FCSTD DOCUMENT  (FreeCAD 0.20R29177 +426 (Git))
Label: ASM_TrussPulley
License: All rights reserved
LicenseURL: http://en.wikipedia.org/wiki/All_rights_reserved
objects: App::Link×7, App::DocumentObjectGroup×3, PartDesign::CoordinateSystem×2, App::FeaturePython×1, App::Part×1
note: 2 computed .brp shape members not serialized (recipe doc carries the construction recipe); baked Part::Feature solids carry a one-line shape summary decoded from their .brp
EXTERNAL_REF file=BreakawayHeadBase.FCStd obj=Sketch
EXTERNAL_REF file=BreakawayHeadTruss.FCStd obj=LCS_Origin
EXTERNAL_REF file=BreakawayHeadTruss.FCStd obj=Assembly
EXTERNAL_REF file=BreakawayHeadTruss.FCStd obj=Pad
EXTERNAL_REF file=BreakawayHeadTruss.FCStd obj=Sketch
EXTERNAL_REF file=CablePulley.FCStd obj=LCS_Origin
EXTERNAL_REF file=CablePulley.FCStd obj=Assembly
EXTERNAL_REF file=Bearing608.FCStd obj=LCS_axle
EXTERNAL_REF file=Bearing608.FCStd obj=Part
EXTERNAL_REF file=CablePulleyBearingHub.FCStd obj=LCS_Origin
EXTERNAL_REF file=CablePulleyBearingHub.FCStd obj=Assembly

FEATURE [App::DocumentObjectGroup] Parts
FEATURE [PartDesign::CoordinateSystem] LCS_Origin
  AttacherType = Attacher::AttachEngine3D
  MapMode = 2
  Support = -> [X_Axis]
FEATURE [App::FeaturePython] Variables  # WARN: FeaturePython — macro-defined, semantics opaque (R4)
  Type = App::PropertyContainer
FEATURE [App::DocumentObjectGroup] Constraints
FEATURE [App::DocumentObjectGroup] Configurations
FEATURE [App::Link] BreakawayHeadTruss
  AttachedBy = #LCS_Origin
  AttachedTo = Parent Assembly#LCS_Origin
  AttachmentOffset = pos=(8,0,0) rot=(0.57735,0.57735,0.57735;2.0944rad)
  LinkPlacement = pos=(8,0,0) rot=(0.57735,0.57735,0.57735;2.0944rad)
  LinkedObject = -> <external BreakawayHeadTruss.FCStd>#Assembly
  Placement = pos=(8,0,0) rot=(0.57735,0.57735,0.57735;2.0944rad)
  SolverId = Asm4EE
  expr: .AttachmentOffset.Base.x = <<BreakawayHeadBase>>#<<Sketch>>.Constraints.EndWidth / 2
  expr: Placement = LCS_Origin.Placement * AttachmentOffset * BreakawayHeadTruss#LCS_Origin.Placement ^ -1
FEATURE [App::Link] BreakawayHeadTruss001
  AttachedBy = #LCS_Origin
  AttachedTo = Parent Assembly#LCS_Origin
  AttachmentOffset = pos=(-10,0,0) rot=(0.57735,0.57735,0.57735;2.0944rad)
  LinkPlacement = pos=(-10,0,0) rot=(0.57735,0.57735,0.57735;2.0944rad)
  LinkedObject = -> <external BreakawayHeadTruss.FCStd>#Assembly
  Placement = pos=(-10,0,0) rot=(0.57735,0.57735,0.57735;2.0944rad)
  SolverId = Asm4EE
  expr: .AttachmentOffset.Base.x = (<<BreakawayHeadBase>>#<<Sketch>>.Constraints.EndWidth / 2 + <<BreakawayHeadTruss>>#<<Pad>>.Length) * -1
  expr: Placement = LCS_Origin.Placement * AttachmentOffset * BreakawayHeadTruss#LCS_Origin.Placement ^ -1
FEATURE [PartDesign::CoordinateSystem] LCS_Pulley
  AttacherType = Attacher::AttachEngine3D
  AttachmentOffset = pos=(0,180,-29.9096) rot=(0,0,1;0rad)
  MapMode = 2
  Placement = pos=(0,180,-29.9096) rot=(0,0,1;0rad)
  Support = -> [LCS_Origin]
  expr: .AttachmentOffset.Base.y = BreakawayHeadTruss#Sketch.Constraints.TrussLength
  expr: .AttachmentOffset.Base.z = BreakawayHeadTruss#Sketch.Constraints.PulleyHoleOffset * -1
FEATURE [App::Link] CablePulley
  AttachedBy = #LCS_Origin
  AttachedTo = Parent Assembly#LCS_Pulley
  AttachmentOffset = pos=(0,0,0) rot=(0,1,0;1.5708rad)
  LinkPlacement = pos=(0,180,-29.9096) rot=(0,1,0;1.5708rad)
  LinkedObject = -> <external CablePulley.FCStd>#Assembly
  Placement = pos=(0,180,-29.9096) rot=(0,1,0;1.5708rad)
  SolverId = Asm4EE
  expr: Placement = LCS_Pulley.Placement * AttachmentOffset * CablePulley#LCS_Origin.Placement ^ -1
FEATURE [App::Link] PulleyBearing
  AssemblyType = Part::Link
  AttachedBy = #LCS_axle
  AttachedTo = Parent Assembly#LCS_Pulley
  AttachmentOffset = pos=(0,0,0) rot=(0,1,0;1.5708rad)
  LinkPlacement = pos=(0,180,-29.9096) rot=(0,1,0;1.5708rad)
  LinkedObject = -> <external Bearing608.FCStd>#Part
  Placement = pos=(0,180,-29.9096) rot=(0,1,0;1.5708rad)
  SolverId = Asm4EE
  expr: Placement = LCS_Pulley.Placement * AttachmentOffset * Bearing608#LCS_axle.Placement ^ -1
FEATURE [App::Link] CablePulleyBearingHub001
  AttachedBy = #LCS_Origin
  AttachedTo = Parent Assembly#LCS_Pulley
  AttachmentOffset = pos=(3.5,0,0) rot=(0,1,0;4.71239rad)
  LinkPlacement = pos=(3.5,180,-29.9096) rot=(0,1,0;4.71239rad)
  LinkedObject = -> <external CablePulleyBearingHub.FCStd>#Assembly
  Placement = pos=(3.5,180,-29.9096) rot=(0,1,0;4.71239rad)
  SolverId = Asm4EE
  expr: Placement = LCS_Pulley.Placement * AttachmentOffset * CablePulleyBearingHub#LCS_Origin.Placement ^ -1
FEATURE [App::Link] CablePulleyBearingHub002
  AttachedBy = #LCS_Origin
  AttachedTo = Parent Assembly#LCS_Pulley
  AttachmentOffset = pos=(-3.5,0,0) rot=(-0.707107,0,-0.707107;3.14159rad)
  LinkPlacement = pos=(-3.5,180,-29.9096) rot=(-0.707107,0,-0.707107;3.14159rad)
  LinkedObject = -> <external CablePulleyBearingHub.FCStd>#Assembly
  Placement = pos=(-3.5,180,-29.9096) rot=(-0.707107,0,-0.707107;3.14159rad)
  SolverId = Asm4EE
  expr: Placement = LCS_Pulley.Placement * AttachmentOffset * CablePulleyBearingHub#LCS_Origin.Placement ^ -1
FEATURE [App::Link] CablePulley001
  AttachedBy = #LCS_Origin
  AttachedTo = Parent Assembly#LCS_Pulley
  AttachmentOffset = pos=(0,0,0) rot=(0,1,0;-1.5708rad)
  LinkPlacement = pos=(0,180,-29.9096) rot=(0,1,0;4.71239rad)
  LinkedObject = -> <external CablePulley.FCStd>#Assembly
  Placement = pos=(0,180,-29.9096) rot=(0,1,0;4.71239rad)
  SolverId = Asm4EE
  expr: Placement = LCS_Pulley.Placement * AttachmentOffset * CablePulley#LCS_Origin.Placement ^ -1
FEATURE [App::Part] Assembly
  AssemblyType = Part::Link
  Group = -> [LCS_Origin,Variables,Constraints,Configurations,BreakawayHeadTruss,BreakawayHeadTruss001,LCS_Pulley,CablePulley,PulleyBearing,CablePulleyBearingHub001,CablePulleyBearingHub002,CablePulley001]
  Origin = -> Origin
  Type = Assembly

RESOLVED EXTERNAL PARTS (link-assembly join: the EXTERNAL_REF files above that resolve inside this repo's crawl, each included once):
---- part Bearing608.FCStd = doc fcstd_2dd5ca27958f ----
FCSTD DOCUMENT  (FreeCAD 0.20R29177 +426 (Git))
Label: Bearing608
License: All rights reserved
LicenseURL: http://en.wikipedia.org/wiki/All_rights_reserved
objects: Sketcher::SketchObject×1, PartDesign::Revolution×1, PartDesign::Chamfer×1, PartDesign::CoordinateSystem×1, App::Part×1
note: 6 computed .brp shape members not serialized (recipe doc carries the construction recipe); baked Part::Feature solids carry a one-line shape summary decoded from their .brp

FEATURE [Sketcher::SketchObject] Sketch
  FullyConstrained = true
  MapMode = 5
  Placement = pos=(0,0,0) rot=(1,0,0;1.5708rad)
  Support = -> [XZ_Plane]
  sketch-geometry (12):
    g0: LineSegment StartX=4 StartY=-3.5 StartZ=0 EndX=5.75 EndY=-3.5 EndZ=0
    g1: LineSegment StartX=11 StartY=-3.5 StartZ=0 EndX=11 EndY=3.5 EndZ=0
    g2: LineSegment StartX=11 StartY=3.5 StartZ=0 EndX=9.25 EndY=3.5 EndZ=0
    g3: LineSegment StartX=4 StartY=3.5 StartZ=0 EndX=4 EndY=-3.5 EndZ=0
    g4: LineSegment StartX=5.75 StartY=3.5 StartZ=0 EndX=6 EndY=3.25 EndZ=0
    g5: LineSegment StartX=6 StartY=3.25 StartZ=0 EndX=9 EndY=3.25 EndZ=0
    g6: LineSegment StartX=9 StartY=3.25 StartZ=0 EndX=9.25 EndY=3.5 EndZ=0
    g7: LineSegment StartX=5.75 StartY=-3.5 StartZ=0 EndX=6 EndY=-3.25 EndZ=0
    g8: LineSegment StartX=6 StartY=-3.25 StartZ=0 EndX=9 EndY=-3.25 EndZ=0
    g9: LineSegment StartX=9 StartY=-3.25 StartZ=0 EndX=9.25 EndY=-3.5 EndZ=0
    g10: LineSegment StartX=5.75 StartY=3.5 StartZ=0 EndX=4 EndY=3.5 EndZ=0
    g11: LineSegment StartX=9.25 StartY=-3.5 StartZ=0 EndX=11 EndY=-3.5 EndZ=0
  constraints (33):
    c: Coincident(g11,g1)
    c: Coincident(g1,g2)
    c: Coincident(g10,g3)
    c: Coincident(g3,g0)
    c: Horizontal(g0)
    c: Horizontal(g2)
    c: Vertical(g1)
    c: DistanceY(g1) = 7
    c: DistanceX(g0) = 4
    c: DistanceX(g11) = 11
    c: Coincident(g4,g5)
    c: Horizontal(g5)
    c: Coincident(g5,g6)
    c: Coincident(g7,g8)
    c: Horizontal(g8)
    c: Coincident(g8,g9)
    c: Coincident(g2,g6)
    c: Coincident(g10,g4)
    c: Tangent(g2,g10)
    c: Coincident(g0,g7)
    c: Coincident(g11,g9)
    c: Tangent(g0,g11)
    c: Equal(g4,g6)
    c: Equal(g6,g7)
    c: Angle(g10,g4) = 2.35619
    c: DistanceX(g2) = -1.75
    c: DistanceX(g10) = -1.75
    c: Equal(g0,g10)
    c: Equal(g11,g2)
    c: Equal(g9,g7)
    c: Parallel(g9,g4)
    c: DistanceY(g5,g1) = 0.25
    c: Symmetric(g0,g3,g-1)
FEATURE [PartDesign::Revolution] Revolution
  AllowMultiFace = false
  Angle = 360
  Axis = (0,-2e-16,1)
  Base = (0,0,0)
  Placement = pos=(0,0,0) rot=(1,0,0;1.5708rad)
  Profile = -> Sketch
  ReferenceAxis = -> Sketch [V_Axis]
  Reversed = true
FEATURE [PartDesign::Chamfer] Chamfer
  Angle = 45
  Base = -> Revolution [Edge3,Edge2,Edge11,Edge12]
  ChamferType = 0
  FlipDirection = false
  Placement = pos=(0,0,0) rot=(1,0,0;1.5708rad)
  Size = 0.25
  Size2 = 1
  SupportTransform = false
  UseAllEdges = false
FEATURE [PartDesign::CoordinateSystem] LCS_axle
  AttacherType = Attacher::AttachEngine3D
  MapMode = 2
  Support = -> [XY_Plane]
FEATURE [App::Part] Part
  Group = -> [Sketch,Revolution,Chamfer,LCS_axle]
  Origin = -> Origin
---- part BreakawayHeadBase.FCStd = doc fcstd_181b5c8611f0 ----
FCSTD DOCUMENT  (FreeCAD 0.20R29177 +426 (Git))
Label: BreakawayHeadBase
License: All rights reserved
LicenseURL: http://en.wikipedia.org/wiki/All_rights_reserved
objects: Sketcher::SketchObject×5, App::DocumentObjectGroup×4, PartDesign::Pocket×4, Part::FeaturePython×4, PartDesign::CoordinateSystem×2, App::Link×2, App::FeaturePython×1, PartDesign::Pad×1, PartDesign::Body×1, App::Part×1
note: 22 computed .brp shape members not serialized (recipe doc carries the construction recipe); baked Part::Feature solids carry a one-line shape summary decoded from their .brp
EXTERNAL_REF file=EndStopTip.FCStd obj=Sketch003
EXTERNAL_REF file=EndStopTip.FCStd obj=Sketch
EXTERNAL_REF file=BreakawayMagnet.FCStd obj=LCS_Origin
EXTERNAL_REF file=BreakawayMagnet.FCStd obj=Assembly

FEATURE [App::DocumentObjectGroup] Parts
FEATURE [PartDesign::CoordinateSystem] LCS_Origin
  AttacherType = Attacher::AttachEngine3D
  MapMode = 2
  Support = -> [X_Axis]
FEATURE [App::FeaturePython] Variables  # WARN: FeaturePython — macro-defined, semantics opaque (R4)
  Type = App::PropertyContainer
FEATURE [App::DocumentObjectGroup] Constraints
FEATURE [App::DocumentObjectGroup] Configurations
FEATURE [Sketcher::SketchObject] Sketch
  FullyConstrained = true
  MapMode = 5
  Support = -> [XY_Plane001]
  expr: Constraints[9] = <<EndStopTip>>#<<SketchChamfer>>.Constraints.MateWidth
  sketch-geometry (14):
    g0: ArcOfCircle CenterX=-10.567 CenterY=-0.5 CenterZ=0 NormalX=0 NormalY=0 NormalZ=1 AngleXU=0 Radius=0.5 StartAngle=1.5708 EndAngle=3.66519
    g1: LineSegment StartX=-10.567 StartY=0 StartZ=0 EndX=10.567 EndY=0 EndZ=0
    g2: ArcOfCircle CenterX=10.567 CenterY=-0.5 CenterZ=0 NormalX=0 NormalY=0 NormalZ=1 AngleXU=0 Radius=0.5 StartAngle=5.75959 EndAngle=7.85398
    g3: LineSegment StartX=11 StartY=-0.75 StartZ=0 EndX=8 EndY=-5.94615 EndZ=0
    g4: LineSegment StartX=-8 StartY=-5.94615 StartZ=0 EndX=-11 EndY=-0.75 EndZ=0
    g5: GeomPoint X=-11.433 Y=0 Z=0
    g6: LineSegment StartX=-8 StartY=-5.94615 StartZ=0 EndX=-8 EndY=-23 EndZ=0
    g7: LineSegment StartX=-7 StartY=-24 StartZ=0 EndX=7 EndY=-24 EndZ=0
    g8: LineSegment StartX=8 StartY=-23 StartZ=0 EndX=8 EndY=-5.94615 EndZ=0
    g9: GeomPoint X=0 Y=-24 Z=0
    g10: ArcOfCircle CenterX=7 CenterY=-23 CenterZ=0 NormalX=0 NormalY=0 NormalZ=1 AngleXU=0 Radius=1 StartAngle=4.71239 EndAngle=6.28319
    g11: GeomPoint X=8 Y=-24 Z=0
    g12: ArcOfCircle CenterX=-7 CenterY=-23 CenterZ=0 NormalX=0 NormalY=0 NormalZ=1 AngleXU=0 Radius=1 StartAngle=3.14159 EndAngle=4.71239
    g13: GeomPoint X=-8 Y=-24 Z=0
  constraints (32):
    c: Tangent(g0,g1) = 1.5708
    c: Tangent(g1,g2) = 1.5708
    c: Tangent(g2,g3) = 1.5708
    c: Tangent(g4,g0) = 1.5708
    c: Horizontal(g1)
    c: Equal(g0,g2)
    c: PointOnObject(g5,g1)
    c: PointOnObject(g5,g4)
    c: Radius(g0) = 0.5
    c: DistanceX(g0,g2) = 22
    c: Symmetric(g1,g0,g-1)
    c: Vertical(g6)
    c: Horizontal(g7)
    c: Vertical(g8)
    c: Symmetric(g13,g11,g9)
    c: PointOnObject(g9,g-2)
    c: Coincident(g4,g6)
    c: Coincident(g8,g3)
    c: Equal(g4,g3)
    c: Angle(g1,g3) = 1.0472
    c: DistanceX(g13,g11) = 16  'EndWidth'
    c: DistanceY(g11,g-1) = 24  'Length'
    c: PointOnObject(g11,g8)
    c: PointOnObject(g11,g7)
    c: Tangent(g8,g10) = -1.5708
    c: Tangent(g7,g10) = -1.5708
    c: PointOnObject(g13,g7)
    c: PointOnObject(g13,g6)
    c: Tangent(g7,g12) = -1.5708
    c: Tangent(g6,g12) = -1.5708
    c: Equal(g12,g10)
    c: Radius(g10) = 1
FEATURE [PartDesign::Pad] Pad
  Direction = (0,0,1)
  Length = 42
  Length2 = 10
  Midplane = true
  Profile = -> Sketch
  ReferenceAxis = -> Sketch [N_Axis]
  Type = 0
  expr: Length = <<EndStopTip>>#<<Sketch>>.Constraints.Height
FEATURE [Sketcher::SketchObject] Sketch001
  FullyConstrained = true
  MapMode = 5
  Placement = pos=(0,0,0) rot=(0.57735,0.57735,0.57735;2.0944rad)
  Support = -> [YZ_Plane001]
  expr: Constraints[25] = <<Sketch>>.Constraints.Length
  sketch-geometry (9):
    g0: LineSegment StartX=-24 StartY=13 StartZ=0 EndX=-34.7696 EndY=13 EndZ=0
    g1: LineSegment StartX=-34.7696 StartY=13 StartZ=0 EndX=-42.3848 EndY=5.38478 EndZ=0
    g2: LineSegment StartX=-42.3848 StartY=5.38478 StartZ=0 EndX=-42.3848 EndY=-5.38478 EndZ=0
    g3: LineSegment StartX=-42.3848 StartY=-5.38478 StartZ=0 EndX=-34.7696 EndY=-13 EndZ=0
    g4: LineSegment StartX=-34.7696 StartY=-13 StartZ=0 EndX=-24 EndY=-13 EndZ=0
    g5: LineSegment StartX=-24 StartY=-13 StartZ=0 EndX=-16.3848 EndY=-5.38478 EndZ=0
    g6: LineSegment StartX=-16.3848 StartY=-5.38478 StartZ=0 EndX=-16.3848 EndY=5.38478 EndZ=0
    g7: LineSegment StartX=-16.3848 StartY=5.38478 StartZ=0 EndX=-24 EndY=13 EndZ=0
    g8: Circle CenterX=-29.3848 CenterY=0 CenterZ=0 NormalX=0 NormalY=0 NormalZ=1 AngleXU=0 Radius=14.0711
  constraints (21):
    c: Coincident(g0,g1)
    c: Coincident(g1,g2)
    c: Coincident(g2,g3)
    c: Coincident(g3,g4)
    c: Coincident(g4,g5)
    c: Coincident(g5,g6)
    c: Coincident(g6,g7)
    c: Coincident(g7,g0)
    c: Equal(g0, g1-g7) x7
    c: PointOnObject(g0,g8)
    c: PointOnObject(g1,g8)
    c: PointOnObject(g2,g8)
    c: PointOnObject(g3,g8)
    c: PointOnObject(g4,g8)
    c: PointOnObject(g5,g8)
    c: PointOnObject(g6,g8)
    c: PointOnObject(g7,g8)
    c: PointOnObject(g8,g-1)
    c: Horizontal(g0)
    c: DistanceX(g4,g-1) = 24
    c: DistanceY(g3,g0) = 26
FEATURE [PartDesign::Pocket] Pocket  label="Cutout"
  BaseFeature = -> Pad
  Direction = (-1,2e-16,-3e-16)
  Length = 5
  Length2 = 5
  Midplane = true
  Profile = -> Sketch001
  ReferenceAxis = -> Sketch001 [N_Axis]
  Type = 1
FEATURE [Sketcher::SketchObject] Sketch002
  FullyConstrained = true
  MapMode = 5
  Placement = pos=(0,0,0) rot=(0.57735,0.57735,0.57735;2.0944rad)
  Support = -> [YZ_Plane001]
  expr: .Constraints.HolesOffset = <<Sketch>>.Constraints.Length - 6mm
  expr: .Constraints.TrussHoleSpacing = <<Pad>>.Length - 10mm
  sketch-geometry (12):
    g0: LineSegment StartX=-18 StartY=16 StartZ=0 EndX=-18 EndY=-16 EndZ=0
    g1: GeomPoint X=-18 Y=0 Z=0
    g2: ArcOfCircle CenterX=-18 CenterY=16 CenterZ=0 NormalX=0 NormalY=0 NormalZ=1 AngleXU=0 Radius=2.15 StartAngle=2.35619 EndAngle=7.06858
    g3: LineSegment StartX=-19.5203 StartY=17.5203 StartZ=0 EndX=-18.8906 EndY=18.15 EndZ=0
    g4: LineSegment StartX=-16.4797 StartY=17.5203 StartZ=0 EndX=-17.1094 EndY=18.15 EndZ=0
    g5: LineSegment StartX=-17.1094 StartY=18.15 StartZ=0 EndX=-18.8906 EndY=18.15 EndZ=0
    g6: ArcOfCircle CenterX=-18 CenterY=16 CenterZ=0 NormalX=0 NormalY=0 NormalZ=1 AngleXU=0 Radius=2.15 StartAngle=0.785398 EndAngle=2.35619
    g7: ArcOfCircle CenterX=-18 CenterY=-16 CenterZ=0 NormalX=0 NormalY=0 NormalZ=1 AngleXU=0 Radius=2.15 StartAngle=2.35619 EndAngle=7.06858
    g8: LineSegment StartX=-19.5203 StartY=-14.4797 StartZ=0 EndX=-18.8906 EndY=-13.85 EndZ=0
    g9: LineSegment StartX=-16.4797 StartY=-14.4797 StartZ=0 EndX=-17.1094 EndY=-13.85 EndZ=0
    g10: LineSegment StartX=-17.1094 StartY=-13.85 StartZ=0 EndX=-18.8906 EndY=-13.85 EndZ=0
    g11: ArcOfCircle CenterX=-18 CenterY=-16 CenterZ=0 NormalX=0 NormalY=0 NormalZ=1 AngleXU=0 Radius=2.15 StartAngle=0.785398 EndAngle=2.35619
  constraints (31):
    c: Vertical(g0)
    c: PointOnObject(g1,g-1)
    c: DistanceY(g0,g0) = 32  'TrussHoleSpacing'
    c: DistanceX(g1,g-1) = 18  'HolesOffset'
    c: Coincident(g2,g0)
    c: Symmetric(g2,g0,g1)
    c: Coincident(g5,g4)
    c: Coincident(g5,g3)
    c: Horizontal(g5)
    c: Tangent(g4,g2) = -1.5708
    c: Tangent(g3,g2) = 1.5708
    c: Diameter(g2) = 4.3
    c: Coincident(g6,g2)
    c: Coincident(g6,g2)
    c: Coincident(g6,g2)
    c: Tangent(g5,g6)
    c: Equal(g4,g3)
    c: Angle(g5,g4) = 2.35619
    c: Coincident(g10,g9)
    c: Coincident(g10,g8)
    c: Horizontal(g10)
    c: Tangent(g9,g7) = -1.5708
    c: Tangent(g8,g7) = 1.5708
    c: Equal(g2,g7) = 5.4
    c: Coincident(g11,g7)
    c: Coincident(g11,g7)
    c: Coincident(g11,g7)
    c: Tangent(g10,g11)
    c: Equal(g9,g8)
    c: Angle(g10,g9) = 2.35619
    c: Coincident(g7,g0)
FEATURE [PartDesign::Pocket] Pocket001  label="TrussHoles"
  BaseFeature = -> Pocket
  Direction = (-1,2e-16,-3e-16)
  Length = 5
  Length2 = 5
  Midplane = true
  Profile = -> Sketch002
  ReferenceAxis = -> Sketch002 [N_Axis]
  Type = 1
FEATURE [Sketcher::SketchObject] Sketch003
  FullyConstrained = true
  MapMode = 5
  Placement = pos=(0,0,0) rot=(1,0,0;1.5708rad)
  Support = -> [XZ_Plane001]
  sketch-geometry (13):
    g0: ArcOfCircle CenterX=0 CenterY=10 CenterZ=0 NormalX=0 NormalY=0 NormalZ=1 AngleXU=0 Radius=9.25 StartAngle=2.35619 EndAngle=3.92699
    g1: ArcOfCircle CenterX=0 CenterY=10 CenterZ=0 NormalX=0 NormalY=0 NormalZ=1 AngleXU=0 Radius=9.25 StartAngle=5.49779 EndAngle=7.06858
    g2: ArcOfCircle CenterX=-9e-16 CenterY=-10 CenterZ=0 NormalX=0 NormalY=0 NormalZ=1 AngleXU=0 Radius=9.25 StartAngle=5.49779 EndAngle=7.06858
    g3: ArcOfCircle CenterX=-9e-16 CenterY=-10 CenterZ=0 NormalX=0 NormalY=0 NormalZ=1 AngleXU=0 Radius=9.25 StartAngle=2.35619 EndAngle=3.92699
    g4: LineSegment StartX=-6.54074 StartY=3.45926 StartZ=0 EndX=-6.54074 EndY=-3.45926 EndZ=0
    g5: LineSegment StartX=6.54074 StartY=3.45926 StartZ=0 EndX=6.54074 EndY=-3.45926 EndZ=0
    g6: LineSegment StartX=6.54074 StartY=-16.5407 StartZ=0 EndX=6.54074 EndY=-22.5407 EndZ=0
    g7: LineSegment StartX=6.54074 StartY=-22.5407 StartZ=0 EndX=-6.54074 EndY=-22.5407 EndZ=0
    g8: LineSegment StartX=-6.54074 StartY=-22.5407 StartZ=0 EndX=-6.54074 EndY=-16.5407 EndZ=0
    g9: LineSegment StartX=-6.54074 StartY=16.5407 StartZ=0 EndX=-6.54074 EndY=22.5407 EndZ=0
    g10: LineSegment StartX=-6.54074 StartY=22.5407 StartZ=0 EndX=6.54074 EndY=22.5407 EndZ=0
    g11: LineSegment StartX=6.54074 StartY=22.5407 StartZ=0 EndX=6.54074 EndY=16.5407 EndZ=0
    g12: LineSegment StartX=-6.54074 StartY=-3.45926 StartZ=0 EndX=-3.08148 EndY=0 EndZ=0
  constraints (39):
    c: PointOnObject(g1,g-2)
    c: Symmetric(g1,g3,g-1)
    c: DistanceY(g3,g1) = 20
    c: Coincident(g1,g0)
    c: Diameter(g1) = 18.5
    c: Coincident(g3,g2)
    c: Coincident(g4,g0)
    c: Coincident(g4,g3)
    c: Coincident(g5,g1)
    c: Coincident(g5,g2)
    c: Coincident(g6,g2)
    c: Vertical(g6)
    c: Coincident(g7,g6)
    c: Horizontal(g7)
    c: Coincident(g8,g3)
    c: Vertical(g8)
    c: Coincident(g9,g0)
    c: Vertical(g9)
    c: Coincident(g10,g9)
    c: Horizontal(g10)
    c: Coincident(g11,g10)
    c: Coincident(g11,g1)
    c: Vertical(g11)
    c: Vertical(g5)
    c: Vertical(g4)
    c: Equal(g0,g1)
    c: Equal(g2,g3)
    c: Equal(g2,g1)
    c: Equal(g6,g8)
    c: Coincident(g8,g7)
    c: Equal(g9,g11)
    c: Equal(g10,g7)
    c: PointOnObject(g2,g6)
    c: PointOnObject(g3,g8)
    c: PointOnObject(g12,g-1)
    c: Tangent(g12,g3) = 1.5708
    c: Angle(g12,g-1) = 2.35619
    c: DistanceY(g11,g11) = 6
    c: Equal(g6,g11)
FEATURE [PartDesign::Pocket] Pocket002  label="MagnetHoles"
  BaseFeature = -> Pocket001
  Direction = (0,1,2e-16)
  Length = 1.5
  Length2 = 5
  Profile = -> Sketch003
  ReferenceAxis = -> Sketch003 [N_Axis]
  Reversed = true
  Type = 0
FEATURE [Sketcher::SketchObject] Sketch004
  FullyConstrained = true
  MapMode = 5
  Placement = pos=(0,0,0) rot=(1,0,0;1.5708rad)
  Support = -> [XZ_Plane001]
  sketch-geometry (8):
    g0: ArcOfCircle CenterX=0 CenterY=10 CenterZ=0 NormalX=0 NormalY=0 NormalZ=1 AngleXU=0 Radius=2.25 StartAngle=2.35619 EndAngle=7.06858
    g1: LineSegment StartX=-1.59099 StartY=11.591 StartZ=0 EndX=-0.931981 EndY=12.25 EndZ=0
    g2: LineSegment StartX=-0.931981 StartY=12.25 StartZ=0 EndX=0.931981 EndY=12.25 EndZ=0
    g3: LineSegment StartX=0.931981 StartY=12.25 StartZ=0 EndX=1.59099 EndY=11.591 EndZ=0
    g4: ArcOfCircle CenterX=0 CenterY=-10 CenterZ=0 NormalX=0 NormalY=0 NormalZ=1 AngleXU=0 Radius=2.25 StartAngle=2.35619 EndAngle=7.06858
    g5: LineSegment StartX=-1.59099 StartY=-8.40901 StartZ=0 EndX=-0.931981 EndY=-7.75 EndZ=0
    g6: LineSegment StartX=-0.931981 StartY=-7.75 StartZ=0 EndX=0.931981 EndY=-7.75 EndZ=0
    g7: LineSegment StartX=0.931981 StartY=-7.75 StartZ=0 EndX=1.59099 EndY=-8.40901 EndZ=0
  constraints (21):
    c: PointOnObject(g0,g-2)
    c: Coincident(g2,g1)
    c: Horizontal(g2)
    c: Coincident(g3,g2)
    c: Tangent(g3,g0) = 1.5708
    c: Tangent(g1,g0) = 1.5708
    c: Equal(g1,g3)
    c: Angle(g2,g3) = 2.35619
    c: Diameter(g0) = 4.5
    c: Tangent(g2,g0)
    c: Coincident(g6,g5)
    c: Horizontal(g6)
    c: Coincident(g7,g6)
    c: Tangent(g7,g4) = 1.5708
    c: Tangent(g5,g4) = 1.5708
    c: Equal(g5,g7)
    c: Angle(g6,g7) = 2.35619
    c: Equal(g0,g4) = 4.5
    c: Tangent(g6,g4)
    c: Symmetric(g4,g0,g-1)
    c: DistanceY(g4,g0) = 20
FEATURE [PartDesign::Pocket] Pocket003  label="MagnetMountHoles"
  BaseFeature = -> Pocket002
  Direction = (0,1,2e-16)
  Length = 16
  Length2 = 5
  Profile = -> Sketch004
  ReferenceAxis = -> Sketch004 [N_Axis]
  Reversed = true
  Type = 0
FEATURE [PartDesign::Body] Body
  Group = -> [Sketch,Pad,Sketch001,Pocket,Sketch002,Pocket001,Sketch003,Pocket002,Sketch004,Pocket003]
  Origin = -> Origin001
  Tip = -> Pocket003
FEATURE [App::Link] BreakawayMagnetTop
  AttachedBy = #LCS_Origin
  AttachedTo = Parent Assembly#LCS_Origin
  AttachmentOffset = pos=(0,-1.5,10) rot=(1,0,0;4.71239rad)
  LinkPlacement = pos=(0,-1.5,10) rot=(1,0,0;4.71239rad)
  LinkedObject = -> <external BreakawayMagnet.FCStd>#Assembly
  Placement = pos=(0,-1.5,10) rot=(1,0,0;4.71239rad)
  SolverId = Asm4EE
  expr: .AttachmentOffset.Base.y = <<MagnetHoles>>.Length * -1
  expr: Placement = LCS_Origin.Placement * AttachmentOffset * BreakawayMagnet#LCS_Origin.Placement ^ -1
FEATURE [App::Link] BreakawayMagnetTop001  label="BreakawayMagnetBottom"
  AttachedBy = #LCS_Origin
  AttachedTo = Parent Assembly#LCS_Origin
  AttachmentOffset = pos=(0,-1.5,-10) rot=(1,0,0;4.71239rad)
  LinkPlacement = pos=(0,-1.5,-10) rot=(1,0,0;4.71239rad)
  LinkedObject = -> <external BreakawayMagnet.FCStd>#Assembly
  Placement = pos=(0,-1.5,-10) rot=(1,0,0;4.71239rad)
  SolverId = Asm4EE
  expr: .AttachmentOffset.Base.y = <<MagnetHoles>>.Length * -1
  expr: Placement = LCS_Origin.Placement * AttachmentOffset * BreakawayMagnet#LCS_Origin.Placement ^ -1
FEATURE [PartDesign::CoordinateSystem] LCS_TrussHoles
  AttacherType = Attacher::AttachEngine3D
  AttachmentOffset = pos=(0,-18,0) rot=(0,0,1;0rad)
  MapMode = 2
  Placement = pos=(0,-18,0) rot=(0,0,1;0rad)
  Support = -> [LCS_Origin]
  expr: .AttachmentOffset.Base.y = <<Sketch002>>.Constraints.HolesOffset * -1
FEATURE [Part::FeaturePython] Screw  label="M4x25-Screw"  # Fasteners workbench fastener (typed FeaturePython)
  Placement = pos=(10,-18,-16) rot=(0,1,0;1.5708rad)
  baseObject = -> Body [Edge93]
  diameter = 5
  invert = false
  leftHanded = false
  length = 7
  lengthCustom = 25
  matchOuter = false
  offset = 2
  thread = false
  type = 45
FEATURE [Part::FeaturePython] Screw001  label="M4x25-Screw001"  # Fasteners workbench fastener (typed FeaturePython)
  Placement = pos=(10,-18,16) rot=(0,1,0;1.5708rad)
  baseObject = -> Body [Edge89]
  diameter = 5
  invert = false
  leftHanded = false
  length = 7
  lengthCustom = 25
  matchOuter = false
  offset = 2
  thread = false
  type = 45
FEATURE [Part::FeaturePython] Nut  label="M4-Nut"  # Fasteners workbench fastener (typed FeaturePython)
  Placement = pos=(-9.6,-18,16) rot=(0,-1,0;1.5708rad)
  baseObject = -> Screw001 [Edge35]
  diameter = 2
  invert = true
  leftHanded = false
  matchOuter = true
  offset = -5
  thread = false
  type = 19
FEATURE [Part::FeaturePython] Nut001  label="M4-Nut001"  # Fasteners workbench fastener (typed FeaturePython)
  Placement = pos=(-9.6,-18,-16) rot=(0,-1,0;1.5708rad)
  baseObject = -> Screw [Edge35]
  diameter = 2
  invert = true
  leftHanded = false
  matchOuter = true
  offset = -5
  thread = false
  type = 19
FEATURE [App::DocumentObjectGroup] Fasteners
  Group = -> [Screw,Screw001,Nut,Nut001]
FEATURE [App::Part] Assembly
  AssemblyType = Part::Link
  Group = -> [LCS_Origin,Variables,Constraints,Configurations,Body,BreakawayMagnetTop,BreakawayMagnetTop001,Fasteners,LCS_TrussHoles,Screw,Screw001,Nut,Nut001]
  Origin = -> Origin
  Type = Assembly
---- part BreakawayHeadTruss.FCStd = doc fcstd_5e5b53ead47f ----
FCSTD DOCUMENT  (FreeCAD 0.20R29177 +426 (Git))
Label: BreakawayHeadTruss
License: All rights reserved
LicenseURL: http://en.wikipedia.org/wiki/All_rights_reserved
objects: App::DocumentObjectGroup×3, Sketcher::SketchObject×2, PartDesign::CoordinateSystem×1, App::FeaturePython×1, PartDesign::Pad×1, PartDesign::Pocket×1, PartDesign::LinearPattern×1, PartDesign::Body×1, App::Part×1
note: 9 computed .brp shape members not serialized (recipe doc carries the construction recipe); baked Part::Feature solids carry a one-line shape summary decoded from their .brp
EXTERNAL_REF file=BreakawayHeadBase.FCStd obj=Sketch002

FEATURE [App::DocumentObjectGroup] Parts
FEATURE [PartDesign::CoordinateSystem] LCS_Origin
  AttacherType = Attacher::AttachEngine3D
  MapMode = 2
  Support = -> [X_Axis]
FEATURE [App::FeaturePython] Variables  # WARN: FeaturePython — macro-defined, semantics opaque (R4)
  CompressionWidth = 8
  InternalRadius = 2
  TensionWidth = 4
  TrussAngle = 15
  Type = App::PropertyContainer
FEATURE [App::DocumentObjectGroup] Constraints
FEATURE [App::DocumentObjectGroup] Configurations
FEATURE [Sketcher::SketchObject] Sketch
  FullyConstrained = true
  MapMode = 5
  Support = -> [XY_Plane001]
  expr: Constraints[35] = <<Variables>>.CompressionWidth
  expr: Constraints[38] = <<Variables>>.TensionWidth
  expr: Constraints[50] = <<Variables>>.TensionWidth
  expr: Constraints[51] = <<Variables>>.CompressionWidth
  expr: Constraints[62] = <<BreakawayHeadBase>>#<<Sketch002>>.Constraints.TrussHoleSpacing
  expr: Constraints[65] = 90 - <<Variables>>.TrussAngle
  sketch-geometry (26):
    g0: Circle CenterX=0 CenterY=0 CenterZ=0 NormalX=0 NormalY=0 NormalZ=1 AngleXU=0 Radius=2.15
    g1: ArcOfCircle CenterX=0 CenterY=0 CenterZ=0 NormalX=0 NormalY=0 NormalZ=1 AngleXU=0 Radius=5 StartAngle=1.5708 EndAngle=2.87979
    g2: ArcOfCircle CenterX=180 CenterY=-29.9096 CenterZ=0 NormalX=0 NormalY=0 NormalZ=1 AngleXU=0 Radius=6 StartAngle=4.71239 EndAngle=7.35705
    g3: ArcOfCircle CenterX=-8.28221 CenterY=-30.9096 CenterZ=0 NormalX=0 NormalY=0 NormalZ=1 AngleXU=0 Radius=5 StartAngle=2.87979 EndAngle=4.71239
    g4: LineSegment StartX=-13.1118 StartY=-29.6155 StartZ=0 EndX=-4.82963 EndY=1.2941 EndZ=0
    g5: LineSegment StartX=180 StartY=-35.9096 StartZ=0 EndX=-8.28221 EndY=-35.9096 EndZ=0
    g6: Circle CenterX=180 CenterY=-29.9096 CenterZ=0 NormalX=0 NormalY=0 NormalZ=1 AngleXU=0 Radius=2.15
    g7: ArcOfCircle CenterX=173.149 CenterY=-26.0427 CenterZ=0 NormalX=0 NormalY=0 NormalZ=1 AngleXU=0 Radius=1.86688 StartAngle=4.71239 EndAngle=7.35705
    g8: ArcOfCircle CenterX=180 CenterY=-29.9096 CenterZ=0 NormalX=0 NormalY=0 NormalZ=1 AngleXU=0 Radius=6 StartAngle=1.07386 EndAngle=4.71239
    g9: LineSegment StartX=130 StartY=-25.9096 StartZ=0 EndX=130 EndY=-3.87784 EndZ=0
    g10: ArcOfCircle CenterX=132 CenterY=-25.9096 CenterZ=0 NormalX=0 NormalY=0 NormalZ=1 AngleXU=0 Radius=2 StartAngle=3.14159 EndAngle=4.71239
    g11: ArcOfCircle CenterX=132 CenterY=-3.87784 CenterZ=0 NormalX=0 NormalY=0 NormalZ=1 AngleXU=0 Radius=2 StartAngle=1.07386 EndAngle=3.14159
    g12: LineSegment StartX=132 StartY=-27.9096 StartZ=0 EndX=173.149 EndY=-27.9096 EndZ=0
    g13: LineSegment StartX=132.953 StartY=-2.11974 StartZ=0 EndX=174.039 EndY=-24.4017 EndZ=0
    g14: LineSegment StartX=182.86 StartY=-24.6353 StartZ=0 EndX=130 EndY=4.03238 EndZ=0
    g15: LineSegment StartX=3e-16 StartY=5 StartZ=0 EndX=126.186 EndY=5 EndZ=0
    g16: LineSegment StartX=174.039 StartY=-24.4017 StartZ=0 EndX=175.946 EndY=-20.8855 EndZ=0
    g17: ArcOfCircle CenterX=126.186 CenterY=-3 CenterZ=0 NormalX=0 NormalY=0 NormalZ=1 AngleXU=0 Radius=8 StartAngle=1.07386 EndAngle=1.5708
    g18: GeomPoint X=128.216 Y=5 Z=0
    g19: LineSegment StartX=8 StartY=1 StartZ=0 EndX=130 EndY=1 EndZ=0
    g20: LineSegment StartX=130 StartY=1 StartZ=0 EndX=130 EndY=-27.9096 EndZ=0
    g21: LineSegment StartX=130 StartY=-27.9096 StartZ=0 EndX=8 EndY=-27.9096 EndZ=0
    g22: LineSegment StartX=8 StartY=-27.9096 StartZ=0 EndX=8 EndY=1 EndZ=0
    g23: GeomPoint X=8 Y=-13.4548 Z=0
    g24: LineSegment StartX=0 StartY=0 StartZ=0 EndX=-8.28221 EndY=-30.9096 EndZ=0
    g25: Circle CenterX=-8.28221 CenterY=-30.9096 CenterZ=0 NormalX=0 NormalY=0 NormalZ=1 AngleXU=0 Radius=2.15
  constraints (68):
    c: Diameter(g0) = 4.3
    c: Tangent(g3,g4) = 1.5708
    c: Tangent(g4,g1) = 1.5708
    c: Horizontal(g5)
    c: DistanceX(g-1,g2) = 180  'TrussLength'
    c: Tangent(g5,g3) = 1.5708
    c: Coincident(g6,g2)
    c: Radius(g1) = 5
    c: Coincident(g1,g0)
    c: Radius(g2) = 6
    c: Coincident(g8,g2)
    c: Coincident(g8,g2)
    c: Vertical(g9)
    c: Tangent(g9,g10) = 1.5708
    c: Tangent(g9,g11) = 1.5708
    c: Tangent(g12,g10) = -1.5708
    c: Tangent(g7,g12) = -1.5708
    c: Tangent(g7,g8)
    c: Tangent(g5,g2) = 1.5708
    c: Coincident(g8,g2)
    c: Horizontal(g12)
    c: Tangent(g13,g7) = 1.5708
    c: Tangent(g13,g11) = 1.5708
    c: Tangent(g14,g2) = -1.5708
    c: Horizontal(g15)
    c: Parallel(g14,g13)
    c: Coincident(g16,g7)
    c: PointOnObject(g16,g14)
    c: Perpendicular(g13,g16)
    c: Tangent(g15,g1) = 1.5708
    c: PointOnObject(g18,g15)
    c: PointOnObject(g18,g14)
    c: Tangent(g15,g17) = 1.5708
    c: Tangent(g14,g17) = -1.5708
    c: Radius(g17) = 8
    c: DistanceY(g3,g10) = 8
    c: Equal(g11,g10)
    c: Radius(g10) = 2
    c: Distance(g16) = 4
    c: DistanceX(g9,g2) = 50
    c: PointOnObject(g14,g9)
    c: Coincident(g19,g20)
    c: Coincident(g20,g21)
    c: Coincident(g21,g22)
    c: Coincident(g22,g19)
    c: Horizontal(g19)
    c: Horizontal(g21)
    c: Vertical(g20)
    c: Vertical(g22)
    c: PointOnObject(g20,g12)
    c: DistanceY(g19,g15) = 4
    c: DistanceX(g0,g19) = 8
    c: DistanceX(g19,g19) = 122  'TrussWidth'
    c: DistanceY(g22,g22) = 28.9096  'TrussHeight'
    c: DistanceX(g-1,g21) = 8  'TrussOffsetX'
    c: Symmetric(g19,g21,g23)
    c: DistanceY(g-1,g23) = -13.4548  'TrussOffsetY'
    c: PointOnObject(g20,g9)
    c: DistanceY(g2,g-1) = 29.9096  'PulleyHoleOffset'
    c: Equal(g3,g1)
    c: Coincident(g24,g0)
    c: Coincident(g24,g3)
    c: Distance(g24) = 32
    c: Coincident(g25,g3)
    c: Equal(g25,g0)
    c: Angle(g-1,g24) = 1.309
    c: Coincident(g0,g-1)
    c: Equal(g6,g25)
FEATURE [PartDesign::Pad] Pad
  Direction = (0,0,1)
  Length = 2
  Length2 = 10
  Profile = -> Sketch
  ReferenceAxis = -> Sketch [N_Axis]
  Type = 0
FEATURE [Sketcher::SketchObject] Sketch_1
  FullyConstrained = true
  MapMode = 2
  Support = -> [XY_Plane001]
  expr: Constraints[10] = Sketch.Constraints.TrussOffsetX
  expr: Constraints[11] = Sketch.Constraints.TrussWidth
  expr: Constraints[12] = Sketch.Constraints.TrussHeight
  expr: Constraints[26] = <<Variables>>.TensionWidth
  expr: Constraints[56] = <<Variables>>.InternalRadius
  expr: Constraints[67] = <<Variables>>.CompressionWidth
  expr: Constraints[9] = Sketch.Constraints.TrussOffsetY
  sketch-geometry (31):
    g0: LineSegment StartX=8 StartY=-27.9096 StartZ=0 EndX=8 EndY=1 EndZ=0
    g1: LineSegment StartX=8 StartY=1 StartZ=0 EndX=130 EndY=1 EndZ=0
    g2: LineSegment StartX=130 StartY=1 StartZ=0 EndX=130 EndY=-27.9096 EndZ=0
    g3: LineSegment StartX=130 StartY=-27.9096 StartZ=0 EndX=8 EndY=-27.9096 EndZ=0
    g4: GeomPoint X=69 Y=-13.4548 Z=0
    g5: LineSegment StartX=10.8863 StartY=-4.01261 StartZ=0 EndX=51.5548 EndY=-24.1167 EndZ=0
    g6: LineSegment StartX=50.6685 StartY=-27.9096 StartZ=0 EndX=10 EndY=-27.9096 EndZ=0
    g7: LineSegment StartX=8 StartY=-25.9096 StartZ=0 EndX=8 EndY=-5.8055 EndZ=0
    g8: LineSegment StartX=17.4452 StartY=-2.79289 StartZ=0 EndX=58.1137 EndY=-22.897 EndZ=0
    g9: LineSegment StartX=61 StartY=-21.1041 StartZ=0 EndX=61 EndY=-1 EndZ=0
    g10: LineSegment StartX=59 StartY=1 StartZ=0 EndX=18.3315 EndY=1 EndZ=0
    g11: LineSegment StartX=59.2274 StartY=-27.9096 StartZ=0 EndX=61 EndY=-24.3238 EndZ=0
    g12: LineSegment StartX=8 StartY=-2.58579 StartZ=0 EndX=9.7726 EndY=1 EndZ=0
    g13: ArcOfCircle CenterX=59 CenterY=-21.1041 CenterZ=0 NormalX=0 NormalY=0 NormalZ=1 AngleXU=0 Radius=2 StartAngle=4.25328 EndAngle=6.28319
    g14: GeomPoint X=61 Y=-24.3238 Z=0
    g15: ArcOfCircle CenterX=59 CenterY=-1 CenterZ=0 NormalX=0 NormalY=0 NormalZ=1 AngleXU=0 Radius=2 StartAngle=0 EndAngle=1.5708
    g16: GeomPoint X=61 Y=1 Z=0
    g17: ArcOfCircle CenterX=18.3315 CenterY=-1 CenterZ=0 NormalX=0 NormalY=0 NormalZ=1 AngleXU=0 Radius=2 StartAngle=1.5708 EndAngle=4.25328
    g18: GeomPoint X=9.7726 Y=1 Z=0
    g19: ArcOfCircle CenterX=10 CenterY=-5.8055 CenterZ=0 NormalX=0 NormalY=0 NormalZ=1 AngleXU=0 Radius=2 StartAngle=1.11169 EndAngle=3.14159
    g20: GeomPoint X=8 Y=-2.58579 Z=0
    g21: ArcOfCircle CenterX=10 CenterY=-25.9096 CenterZ=0 NormalX=0 NormalY=0 NormalZ=1 AngleXU=0 Radius=2 StartAngle=3.14159 EndAngle=4.71239
    g22: GeomPoint X=8 Y=-27.9096 Z=0
    g23: ArcOfCircle CenterX=50.6685 CenterY=-25.9096 CenterZ=0 NormalX=0 NormalY=0 NormalZ=1 AngleXU=0 Radius=2 StartAngle=4.71239 EndAngle=7.39487
    g24: GeomPoint X=59.2274 Y=-27.9096 Z=0
    g25: LineSegment StartX=8 StartY=-27.9096 StartZ=0 EndX=8 EndY=-37.9096 EndZ=0
    g26: LineSegment StartX=8 StartY=-37.9096 StartZ=0 EndX=69 EndY=-37.9096 EndZ=0
    g27: LineSegment StartX=61 StartY=-21.1041 StartZ=0 EndX=69 EndY=-21.1041 EndZ=0
    g28: LineSegment StartX=69 StartY=-21.1041 StartZ=0 EndX=69 EndY=-37.9096 EndZ=0
    g29: LineSegment StartX=69 StartY=-37.9096 StartZ=0 EndX=130 EndY=-37.9096 EndZ=0
    g30: LineSegment StartX=130 StartY=-37.9096 StartZ=0 EndX=130 EndY=-27.9096 EndZ=0
  constraints (74):
    c: Coincident(g0,g1)
    c: Coincident(g1,g2)
    c: Coincident(g2,g3)
    c: Coincident(g3,g0)
    c: Horizontal(g1)
    c: Horizontal(g3)
    c: Vertical(g0)
    c: Vertical(g2)
    c: Symmetric(g1,g0,g4)
    c: DistanceY(g-1,g4) = -13.4548
    c: DistanceX(g-1,g0) = 8
    c: DistanceX(g1,g1) = 122
    c: DistanceY(g0,g0) = 28.9096
    c: PointOnObject(g20,g0)
    c: PointOnObject(g24,g3)
    c: Coincident(g22,g0)
    c: PointOnObject(g18,g1)
    c: PointOnObject(g16,g1)
    c: Vertical(g9)
    c: Parallel(g8,g5)
    c: Coincident(g11,g24)
    c: Coincident(g11,g14)
    c: Coincident(g12,g20)
    c: Coincident(g12,g18)
    c: Parallel(g11,g12)
    c: Perpendicular(g5,g11)
    c: Distance(g11) = 4
    c: PointOnObject(g14,g8)
    c: PointOnObject(g14,g9)
    c: Tangent(g8,g13) = -1.5708
    c: Tangent(g9,g13) = -1.5708
    c: PointOnObject(g16,g9)
    c: PointOnObject(g16,g10)
    c: Tangent(g9,g15) = -1.5708
    c: Tangent(g10,g15) = -1.5708
    c: PointOnObject(g18,g10)
    c: PointOnObject(g18,g8)
    c: Tangent(g10,g17) = -1.5708
    c: Tangent(g8,g17) = -1.5708
    c: PointOnObject(g20,g5)
    c: PointOnObject(g20,g7)
    c: Tangent(g5,g19) = 1.5708
    c: Tangent(g7,g19) = 1.5708
    c: PointOnObject(g22,g7)
    c: PointOnObject(g22,g6)
    c: Tangent(g7,g21) = 1.5708
    c: Tangent(g6,g21) = 1.5708
    c: PointOnObject(g24,g6)
    c: PointOnObject(g24,g5)
    c: Tangent(g6,g23) = 1.5708
    c: Tangent(g5,g23) = 1.5708
    c: Equal(g23,g21)
    c: Equal(g21,g19)
    c: Equal(g19,g17)
    c: Equal(g17,g15)
    c: Equal(g15,g13)
    c: Radius(g15) = 2
    c: Coincident(g25,g0)
    c: Vertical(g25)
    c: Coincident(g26,g25)
    c: Horizontal(g26)
    c: DistanceY(g25,g25) = 10
    c: Coincident(g27,g9)
    c: Horizontal(g27)
    c: Coincident(g28,g27)
    c: Coincident(g28,g26)
    c: Vertical(g28)
    c: DistanceX(g27,g27) = 8
    c: Horizontal(g29)
    c: Coincident(g30,g29)
    c: Coincident(g30,g2)
    c: Vertical(g30)
    c: Coincident(g29,g26)
    c: Equal(g26,g29)
FEATURE [PartDesign::Pocket] Pocket  label="TrussCutout"
  BaseFeature = -> Pad
  Direction = (0,0,-1)
  Length = 5
  Length2 = 5
  Midplane = true
  Profile = -> Sketch_1
  ReferenceAxis = -> Sketch_1 [N_Axis]
  Type = 1
FEATURE [PartDesign::LinearPattern] LinearPattern  label="CutoutPattern"
  BaseFeature = -> Pocket
  Direction = -> Sketch_1 [H_Axis]
  Length = 61
  Occurrences = 2
  Originals = -> [Pocket]
  expr: Length = Sketch.Constraints.TrussWidth * 0.5
FEATURE [PartDesign::Body] Body
  Group = -> [Sketch,Pad,Sketch_1,Pocket,LinearPattern]
  Origin = -> Origin001
  Tip = -> LinearPattern
FEATURE [App::Part] Assembly
  AssemblyType = Part::Link
  Group = -> [LCS_Origin,Variables,Constraints,Configurations,Body]
  Origin = -> Origin
  Type = Assembly
---- part CablePulley.FCStd = doc fcstd_129e9fe7581f ----
FCSTD DOCUMENT  (FreeCAD 0.20R29177 +426 (Git))
Label: CablePulley
License: All rights reserved
LicenseURL: http://en.wikipedia.org/wiki/All_rights_reserved
objects: App::DocumentObjectGroup×3, Sketcher::SketchObject×3, PartDesign::CoordinateSystem×1, App::FeaturePython×1, PartDesign::Revolution×1, PartDesign::Pocket×1, PartDesign::PolarPattern×1, PartDesign::Body×1, App::Part×1
note: 10 computed .brp shape members not serialized (recipe doc carries the construction recipe); baked Part::Feature solids carry a one-line shape summary decoded from their .brp
EXTERNAL_REF file=Params.FCStd obj=Spreadsheet

FEATURE [App::DocumentObjectGroup] Parts
FEATURE [PartDesign::CoordinateSystem] LCS_Origin
  AttacherType = Attacher::AttachEngine3D
  MapMode = 2
  Support = -> [X_Axis]
FEATURE [App::FeaturePython] Variables  # WARN: FeaturePython — macro-defined, semantics opaque (R4)
  InnerDiameter = 22.3
  NumSpokes = 5
  OuterDiameter = 120
  Type = App::PropertyContainer
  expr: OuterDiameter = <<Params>>#<<Params>>.CablePulleyDiameter
FEATURE [App::DocumentObjectGroup] Constraints
FEATURE [App::DocumentObjectGroup] Configurations
FEATURE [Sketcher::SketchObject] Sketch
  FullyConstrained = true
  MapMode = 5
  Support = -> [XY_Plane001]
  expr: Constraints[2] = <<Variables>>.OuterDiameter
  expr: Constraints[3] = <<Variables>>.InnerDiameter
  sketch-geometry (2):
    g0: Circle CenterX=0 CenterY=0 CenterZ=0 NormalX=0 NormalY=0 NormalZ=1 AngleXU=0 Radius=11.15
    g1: Circle CenterX=0 CenterY=0 CenterZ=0 NormalX=0 NormalY=0 NormalZ=1 AngleXU=0 Radius=60
  constraints (4):
    c: Coincident(g0,g-1)
    c: Coincident(g1,g0)
    c: Diameter(g1) = 120
    c: Diameter(g0) = 22.3
FEATURE [Sketcher::SketchObject] Sketch001
  FullyConstrained = true
  MapMode = 5
  Support = -> [XY_Plane001]
  expr: Constraints[16] = <<Variables>>.InnerDiameter + 6
  expr: Constraints[38] = 180 / <<Variables>>.NumSpokes
  expr: Constraints[4] = <<Variables>>.OuterDiameter / 2 - 2
  sketch-geometry (37):
    g0: LineSegment StartX=-5.12151 StartY=16.6459 StartZ=0 EndX=-2.81551 EndY=30.9437 EndZ=0
    g1: LineSegment StartX=-8.31716 StartY=11.4476 StartZ=0 EndX=-34.0915 EndY=46.923 EndZ=0
    g2: LineSegment StartX=-6.25073 StartY=38.8571 StartZ=0 EndX=-21.7057 EndY=49.2449 EndZ=0
    g3: LineSegment StartX=-20.4235 StartY=50.7915 StartZ=0 EndX=-4 EndY=41.3094 EndZ=0
    g4: LineSegment StartX=4 StartY=41.3094 StartZ=0 EndX=20.4235 EndY=50.7915 EndZ=0
    g5: LineSegment StartX=5.12151 StartY=16.6459 StartZ=0 EndX=2.81551 EndY=30.9437 EndZ=0
    g6: LineSegment StartX=6.25073 StartY=38.8571 StartZ=0 EndX=21.7057 EndY=49.2449 EndZ=0
    g7: LineSegment StartX=8.31716 StartY=11.4476 StartZ=0 EndX=34.0915 EndY=46.923 EndZ=0
    g8: ArcOfCircle CenterX=0 CenterY=0 CenterZ=0 NormalX=0 NormalY=0 NormalZ=1 AngleXU=0 Radius=58 StartAngle=0.942478 EndAngle=1.02
    g9: ArcOfCircle CenterX=0 CenterY=0 CenterZ=0 NormalX=0 NormalY=0 NormalZ=1 AngleXU=0 Radius=58 StartAngle=2.1216 EndAngle=2.19911
    g10: ArcOfCircle CenterX=0 CenterY=0 CenterZ=0 NormalX=0 NormalY=0 NormalZ=1 AngleXU=0 Radius=58 StartAngle=1.21659 EndAngle=1.92501
    g11: LineSegment StartX=-2 StartY=36 StartZ=0 EndX=2 EndY=36 EndZ=0
    g12: GeomPoint X=0 Y=36 Z=0
    g13: LineSegment StartX=-6.38814 StartY=8.79251 StartZ=0 EndX=6.38814 EndY=8.79251 EndZ=0
    g14: Circle CenterX=0 CenterY=0 CenterZ=0 NormalX=0 NormalY=0 NormalZ=1 AngleXU=0 Radius=14.15
    g15: ArcOfCircle CenterX=13.0194 CenterY=17.9197 CenterZ=0 NormalX=0 NormalY=0 NormalZ=1 AngleXU=0 Radius=8 StartAngle=3.3015 EndAngle=4.08407
    g16: GeomPoint X=6.38814 Y=8.79251 Z=0
    g17: ArcOfCircle CenterX=-13.0194 CenterY=17.9197 CenterZ=0 NormalX=0 NormalY=0 NormalZ=1 AngleXU=0 Radius=8 StartAngle=5.34071 EndAngle=6.12328
    g18: GeomPoint X=-6.38814 Y=8.79251 Z=0
    g19: LineSegment StartX=8.31716 StartY=11.4476 StartZ=0 EndX=0 EndY=17.4904 EndZ=0
    g20: LineSegment StartX=-8.31716 StartY=11.4476 StartZ=0 EndX=0 EndY=17.4904 EndZ=0
    g21: ArcOfCircle CenterX=10.7134 CenterY=32.2175 CenterZ=0 NormalX=0 NormalY=0 NormalZ=1 AngleXU=0 Radius=8 StartAngle=2.16258 EndAngle=3.3015
    g22: GeomPoint X=2 Y=36 Z=0
    g23: ArcOfCircle CenterX=6e-15 CenterY=48.2376 CenterZ=0 NormalX=0 NormalY=0 NormalZ=1 AngleXU=0 Radius=8 StartAngle=4.18879 EndAngle=5.23599
    g24: GeomPoint X=0 Y=39 Z=0
    g25: ArcOfCircle CenterX=-10.7134 CenterY=32.2175 CenterZ=0 NormalX=0 NormalY=0 NormalZ=1 AngleXU=0 Radius=8 StartAngle=6.12328 EndAngle=7.2622
    g26: GeomPoint X=-2 Y=36 Z=0
    g27: ArcOfCircle CenterX=26.1684 CenterY=42.6053 CenterZ=0 NormalX=0 NormalY=0 NormalZ=1 AngleXU=0 Radius=8 StartAngle=1.02 EndAngle=2.16258
    g28: ArcOfCircle CenterX=19.4235 CenterY=52.5236 CenterZ=0 NormalX=0 NormalY=0 NormalZ=1 AngleXU=0 Radius=2 StartAngle=5.23599 EndAngle=7.49977
    g29: ArcOfCircle CenterX=-19.4235 CenterY=52.5236 CenterZ=0 NormalX=0 NormalY=0 NormalZ=1 AngleXU=0 Radius=2 StartAngle=1.92501 EndAngle=4.18879
    g30: ArcOfCircle CenterX=-26.1684 CenterY=42.6053 CenterZ=0 NormalX=0 NormalY=0 NormalZ=1 AngleXU=0 Radius=8 StartAngle=0.979016 EndAngle=2.1216
    g31: LineSegment StartX=4.87131 StartY=39.9125 StartZ=0 EndX=24.88 EndY=52.3926 EndZ=0
    g32: LineSegment StartX=20.4235 StartY=50.7915 StartZ=0 EndX=20.9528 EndY=49.943 EndZ=0
    g33: ArcOfCircle CenterX=0 CenterY=0 CenterZ=0 NormalX=0 NormalY=0 NormalZ=1 AngleXU=0 Radius=58 StartAngle=1.02 EndAngle=1.21659
    g34: LineSegment StartX=4.87131 StartY=39.9125 StartZ=0 EndX=4 EndY=41.3094 EndZ=0
    g35: LineSegment StartX=4.87131 StartY=39.9125 StartZ=0 EndX=5.74262 EndY=38.5156 EndZ=0
    g36: LineSegment StartX=20.9528 StartY=49.943 StartZ=0 EndX=21.482 EndY=49.0946 EndZ=0
  constraints (90):
    c: PointOnObject(g24,g-2)
    c: Coincident(g8,g7)
    c: Coincident(g9,g1)
    c: Equal(g10,g9)
    c: Radius(g10) = 58
    c: Coincident(g11,g26)
    c: Coincident(g11,g22)
    c: Horizontal(g11)
    c: Symmetric(g26,g22,g12)
    c: PointOnObject(g12,g-2)
    c: Horizontal(g13)
    c: DistanceY(g12,g24) = 3
    c: DistanceX(g11,g11) = 4
    c: Coincident(g16,g13)
    c: Coincident(g18,g13)
    c: Coincident(g14,g8)
    c: Diameter(g14) = 28.3
    c: PointOnObject(g8,g1)
    c: PointOnObject(g8,g7)
    c: Coincident(g8,g9)
    c: Coincident(g8,g10)
    c: Coincident(g8,g-1)
    c: PointOnObject(g16,g7)
    c: PointOnObject(g16,g5)
    c: Tangent(g5,g15) = 1.5708
    c: PointOnObject(g18,g0)
    c: PointOnObject(g18,g1)
    c: Tangent(g0,g17) = -1.5708
    c: Equal(g15,g17)
    c: Radius(g15) = 8
    c: PointOnObject(g19,g-2)
    c: Tangent(g19,g15) = 1.5708
    c: Coincident(g15,g7)
    c: Perpendicular(g7,g19)
    c: Coincident(g20,g19)
    c: Tangent(g20,g17) = -1.5708
    c: Coincident(g1,g17)
    c: Perpendicular(g20,g1)
    c: Angle(g7,g-2) = 0.628319
    c: PointOnObject(g7,g14)
    c: PointOnObject(g22,g5)
    c: PointOnObject(g22,g6)
    c: Tangent(g5,g21) = 1.5708
    c: Tangent(g6,g21) = 1.5708
    c: PointOnObject(g24,g4)
    c: PointOnObject(g24,g3)
    c: Tangent(g4,g23) = -1.5708
    c: Tangent(g3,g23) = -1.5708
    c: PointOnObject(g26,g0)
    c: PointOnObject(g26,g2)
    c: Tangent(g0,g25) = -1.5708
    c: Tangent(g2,g25) = -1.5708
    c: Equal(g21,g25)
    c: Equal(g25,g23)
    c: Radius(g23) = 8
    c: Equal(g4,g3)
    c: Equal(g6,g2)
    c: Tangent(g6,g27) = 1.5708
    c: Tangent(g8,g27) = -1.5708
    c: Tangent(g4,g28) = -1.5708
    c: Tangent(g10,g28) = -1.5708
    c: Tangent(g3,g29) = -1.5708
    c: Tangent(g10,g29) = -1.5708
    c: Tangent(g2,g30) = -1.5708
    c: Tangent(g9,g30) = -1.5708
    c: Radius(g28) = 2
    c: Coincident(g32,g4)
    c: PointOnObject(g32,g31)
    c: Coincident(g33,g8)
    c: Coincident(g33,g8)
    c: Coincident(g33,g10)
    c: PointOnObject(g31,g33)
    c: Coincident(g34,g31)
    c: Coincident(g34,g4)
    c: Coincident(g35,g31)
    c: PointOnObject(g35,g6)
    c: Parallel(g35,g34)
    c: Equal(g35,g34)
    c: Perpendicular(g34,g31)
    c: Coincident(g36,g32)
    c: PointOnObject(g36,g6)
    c: Parallel(g36,g32)
    c: Perpendicular(g31,g32)
    c: Equal(g36,g32)
    c: Distance(g36,g4) = 2
    c: Angle(g4,g3) = 2.0944
    c: Equal(g27,g30)
    c: Radius(g27) = 8
    c: Equal(g28,g29)
    c: DistanceY(g8,g12) = 36
FEATURE [Sketcher::SketchObject] Sketch002
  FullyConstrained = true
  MapMode = 5
  Placement = pos=(0,0,0) rot=(1,0,0;1.5708rad)
  Support = -> [XZ_Plane001]
  expr: Constraints[5] = <<Params>>#<<Params>>.CablePulleyDiameter / 2
  expr: Constraints[6] = <<Variables>>.InnerDiameter / 2
  sketch-geometry (11):
    g0: LineSegment StartX=-11.15 StartY=0 StartZ=0 EndX=-11.15 EndY=3.5 EndZ=0
    g1: LineSegment StartX=-11.15 StartY=0 StartZ=0 EndX=-61.2426 EndY=0 EndZ=0
    g2: ArcOfCircle CenterX=-64.2426 CenterY=3 CenterZ=0 NormalX=0 NormalY=0 NormalZ=1 AngleXU=0 Radius=4.24264 StartAngle=5.49779 EndAngle=7.06858
    g3: GeomPoint X=-11.15 Y=1.75 Z=0
    g4: GeomPoint X=-60 Y=2.99999 Z=0
    g5: LineSegment StartX=-60 StartY=2.99999 StartZ=0 EndX=-60 EndY=0 EndZ=0
    g6: LineSegment StartX=-61.2426 StartY=6 StartZ=0 EndX=-61.2426 EndY=0 EndZ=0
    g7: LineSegment StartX=-61.2426 StartY=6 StartZ=0 EndX=-59.2426 EndY=6 EndZ=0
    g8: LineSegment StartX=-59.2426 StartY=6 StartZ=0 EndX=-56.7426 EndY=3.5 EndZ=0
    g9: LineSegment StartX=-56.7426 StartY=3.5 StartZ=0 EndX=-11.15 EndY=3.5 EndZ=0
    g10: LineSegment StartX=-61.2426 StartY=6 StartZ=0 EndX=-55.2426 EndY=0 EndZ=0
  constraints (29):
    c: Vertical(g0)
    c: Coincident(g1,g0)
    c: Horizontal(g1)
    c: Coincident(g2,g1)
    c: Symmetric(g0,g0,g3)
    c: DistanceX(g4,g-1) = 60
    c: DistanceX(g3,g-1) = 11.15
    c: PointOnObject(g4,g2)
    c: Coincident(g5,g4)
    c: Vertical(g5)
    c: Tangent(g5,g2)
    c: PointOnObject(g5,g-1)
    c: PointOnObject(g1,g-1)
    c: Coincident(g6,g1)
    c: Vertical(g6)
    c: DistanceY(g6,g6) = 6
    c: Coincident(g2,g6)
    c: Coincident(g7,g2)
    c: Horizontal(g7)
    c: DistanceX(g7,g7) = 2
    c: Coincident(g8,g7)
    c: Coincident(g9,g8)
    c: Coincident(g9,g0)
    c: Horizontal(g9)
    c: Angle(g-1,g8) = 2.35619
    c: PointOnObject(g10,g1)
    c: Tangent(g10,g2) = 1.5708
    c: Angle(g6,g10) = 0.785398
    c: DistanceY(g0,g0) = 3.5
FEATURE [PartDesign::Revolution] Revolution  label="Groove"
  Angle = 360
  Axis = (0,-2e-16,1)
  Base = (0,0,0)
  Placement = pos=(0,0,0) rot=(1,0,0;1.5708rad)
  Profile = -> Sketch002
  ReferenceAxis = -> Sketch002 [V_Axis]
FEATURE [PartDesign::Pocket] Pocket  label="Spoke"
  BaseFeature = -> Revolution
  Direction = (0,0,-1)
  Length = 5
  Length2 = 5
  Midplane = true
  Placement = pos=(0,0,0) rot=(1,0,0;1.5708rad)
  Profile = -> Sketch001
  ReferenceAxis = -> Sketch001 [N_Axis]
  Type = 1
FEATURE [PartDesign::PolarPattern] PolarPattern
  Angle = 360
  Axis = -> Sketch001 [N_Axis]
  BaseFeature = -> Pocket
  Occurrences = 5
  Originals = -> [Pocket]
  Placement = pos=(0,0,0) rot=(1,0,0;1.5708rad)
  expr: Occurrences = <<Variables>>.NumSpokes
FEATURE [PartDesign::Body] Body
  Group = -> [Sketch,Revolution,Sketch001,Pocket,PolarPattern,Sketch002]
  Origin = -> Origin001
  Tip = -> PolarPattern
FEATURE [App::Part] Assembly
  AssemblyType = Part::Link
  Group = -> [LCS_Origin,Variables,Constraints,Configurations,Body]
  Origin = -> Origin
  Type = Assembly
---- part CablePulleyBearingHub.FCStd = doc fcstd_0c9685749e9f ----
FCSTD DOCUMENT  (FreeCAD 0.20R29177 +426 (Git))
Label: CablePulleyBearingHub
License: All rights reserved
LicenseURL: http://en.wikipedia.org/wiki/All_rights_reserved
objects: App::DocumentObjectGroup×3, PartDesign::CoordinateSystem×1, App::FeaturePython×1, Sketcher::SketchObject×1, PartDesign::Revolution×1, PartDesign::Body×1, App::Part×1
note: 5 computed .brp shape members not serialized (recipe doc carries the construction recipe); baked Part::Feature solids carry a one-line shape summary decoded from their .brp

FEATURE [App::DocumentObjectGroup] Parts
FEATURE [PartDesign::CoordinateSystem] LCS_Origin
  AttacherType = Attacher::AttachEngine3D
  MapMode = 2
  Support = -> [X_Axis]
FEATURE [App::FeaturePython] Variables  # WARN: FeaturePython — macro-defined, semantics opaque (R4)
  Type = App::PropertyContainer
FEATURE [App::DocumentObjectGroup] Constraints
FEATURE [App::DocumentObjectGroup] Configurations
FEATURE [Sketcher::SketchObject] Sketch
  FullyConstrained = true
  MapMode = 5
  Placement = pos=(0,0,0) rot=(1,0,0;1.5708rad)
  Support = -> [XZ_Plane001]
  sketch-geometry (6):
    g0: LineSegment StartX=2.25 StartY=-4.5 StartZ=0 EndX=2.25 EndY=3.2 EndZ=0
    g1: LineSegment StartX=2.25 StartY=3.2 StartZ=0 EndX=3.9 EndY=3.2 EndZ=0
    g2: LineSegment StartX=3.9 StartY=3.2 StartZ=0 EndX=3.9 EndY=0 EndZ=0
    g3: LineSegment StartX=3.9 StartY=0 StartZ=0 EndX=5.9 EndY=0 EndZ=0
    g4: LineSegment StartX=5.9 StartY=0 StartZ=0 EndX=5.9 EndY=-4.5 EndZ=0
    g5: LineSegment StartX=5.9 StartY=-4.5 StartZ=0 EndX=2.25 EndY=-4.5 EndZ=0
  constraints (18):
    c: Vertical(g0)
    c: Coincident(g0,g1)
    c: Horizontal(g1)
    c: Coincident(g1,g2)
    c: Vertical(g2)
    c: Coincident(g2,g3)
    c: Horizontal(g3)
    c: Coincident(g3,g4)
    c: Vertical(g4)
    c: Coincident(g4,g5)
    c: Coincident(g5,g0)
    c: Horizontal(g5)
    c: DistanceX(g-1,g0) = 2.25
    c: DistanceX(g-1,g1) = 3.9
    c: DistanceX(g3,g3) = 2
    c: DistanceY(g4,g4) = 4.5
    c: DistanceY(g2,g2) = 3.2
    c: PointOnObject(g2,g-1)
FEATURE [PartDesign::Revolution] Revolution
  Angle = 360
  Axis = (0,-2e-16,1)
  Base = (0,0,0)
  Placement = pos=(0,0,0) rot=(1,0,0;1.5708rad)
  Profile = -> Sketch
  ReferenceAxis = -> Sketch [V_Axis]
  Reversed = true
FEATURE [PartDesign::Body] Body
  Group = -> [Sketch,Revolution]
  Origin = -> Origin001
  Tip = -> Revolution
FEATURE [App::Part] Assembly
  AssemblyType = Part::Link
  Group = -> [LCS_Origin,Variables,Constraints,Configurations,Body]
  Origin = -> Origin
  Type = Assembly
